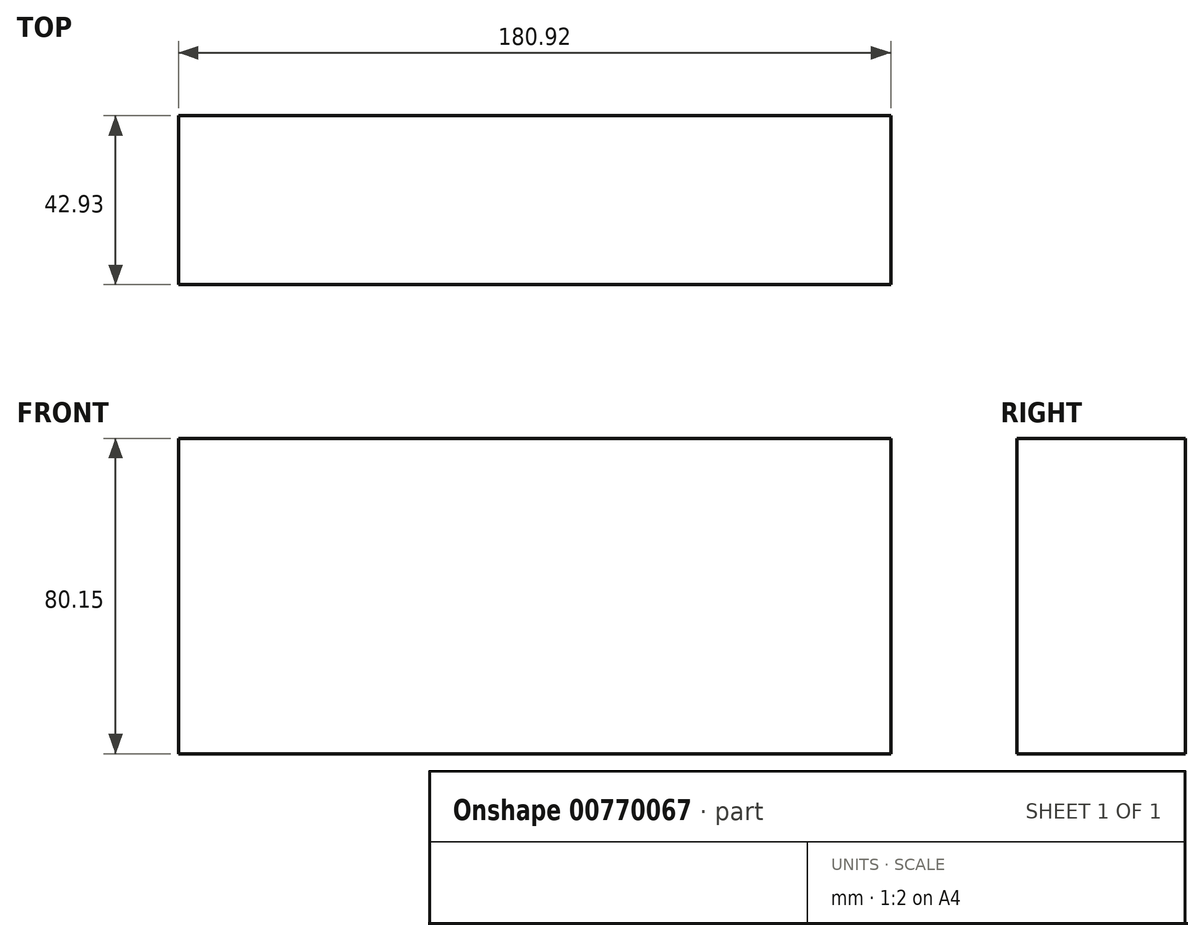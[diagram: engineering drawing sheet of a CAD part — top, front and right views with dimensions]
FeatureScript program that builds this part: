
annotation { "Feature Type Name" : "Feature", "Feature Type Description" : "" }
export const myFeature = defineFeature(function(context is Context, id is Id, definition is map)
    precondition{}
    {
        {
            var Q0;
            Q0=qCreatedBy(makeId("Front.planeOp"),FACE);
            var sketch = newSketch(context, id + "F0", { "sketchPlane" : qUnion([Q0])});
            skLineSegment(sketch, "E0.bottom", {"start": v(-139.78, 42.7) * mm, "end": v(41.14, 42.7) * mm});
            skLineSegment(sketch, "E0.top", {"start": v(-139.78, -37.45) * mm, "end": v(41.14, -37.45) * mm});
            skLineSegment(sketch, "E0.left", {"start": v(-139.78, 42.7) * mm, "end": v(-139.78, -37.45) * mm});
            skLineSegment(sketch, "E0.right", {"start": v(41.14, 42.7) * mm, "end": v(41.14, -37.45) * mm});
            skSolve(sketch);
        }
        {
            var Q0;
            Q0 = qSketchRegion(id + "F0", true);
            extrude(context, id + "F1", {"entities" : qUnion([Q0]), "depth" : 42.93 * mm, "offsetDistance" : 25.4 * mm});
        }
    });
